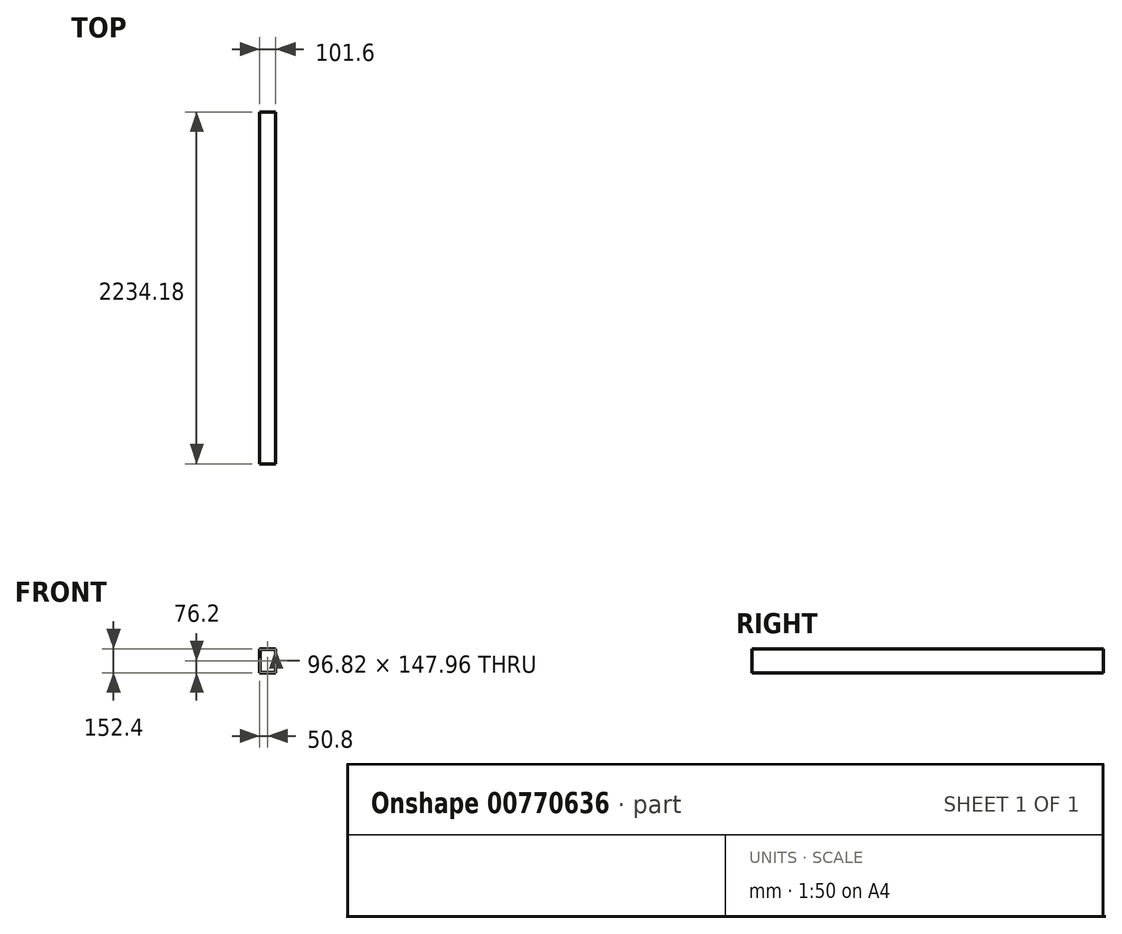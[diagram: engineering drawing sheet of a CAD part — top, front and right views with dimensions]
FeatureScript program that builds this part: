
annotation { "Feature Type Name" : "Feature", "Feature Type Description" : "" }
export const myFeature = defineFeature(function(context is Context, id is Id, definition is map)
    precondition{}
    {
        {
            var Q0;
            Q0=qCreatedBy(makeId("Front.planeOp"),FACE);
            var sketch = newSketch(context, id + "F0", { "sketchPlane" : qUnion([Q0])});
            skLineSegment(sketch, "E0.bottom", {"start": v(50.8, -76.2) * mm, "end": v(-50.8, -76.2) * mm});
            skLineSegment(sketch, "E0.top", {"start": v(50.8, 76.2) * mm, "end": v(-50.8, 76.2) * mm});
            skLineSegment(sketch, "E0.left", {"start": v(50.8, -76.2) * mm, "end": v(50.8, 76.2) * mm});
            skLineSegment(sketch, "E0.right", {"start": v(-50.8, -76.2) * mm, "end": v(-50.8, 76.2) * mm});
            skPoint(sketch, "E0.middle", {"position": v(0, 0) * mm});
            skLineSegment(sketch, "E1.bottom", {"start": v(48.41, -73.98) * mm, "end": v(-48.41, -73.98) * mm});
            skLineSegment(sketch, "E1.top", {"start": v(48.41, 73.98) * mm, "end": v(-48.41, 73.98) * mm});
            skLineSegment(sketch, "E1.left", {"start": v(48.41, -73.98) * mm, "end": v(48.41, 73.98) * mm});
            skLineSegment(sketch, "E1.right", {"start": v(-48.41, -73.98) * mm, "end": v(-48.41, 73.98) * mm});
            skSolve(sketch);
        }
        {
            var Q0;
            Q0 = qSketchRegion(id + "F0", true);
            extrude(context, id + "F1", {"entities" : qUnion([Q0]), "depth" : 2234.18 * mm, "offsetDistance" : 25.4 * mm});
        }
    });
